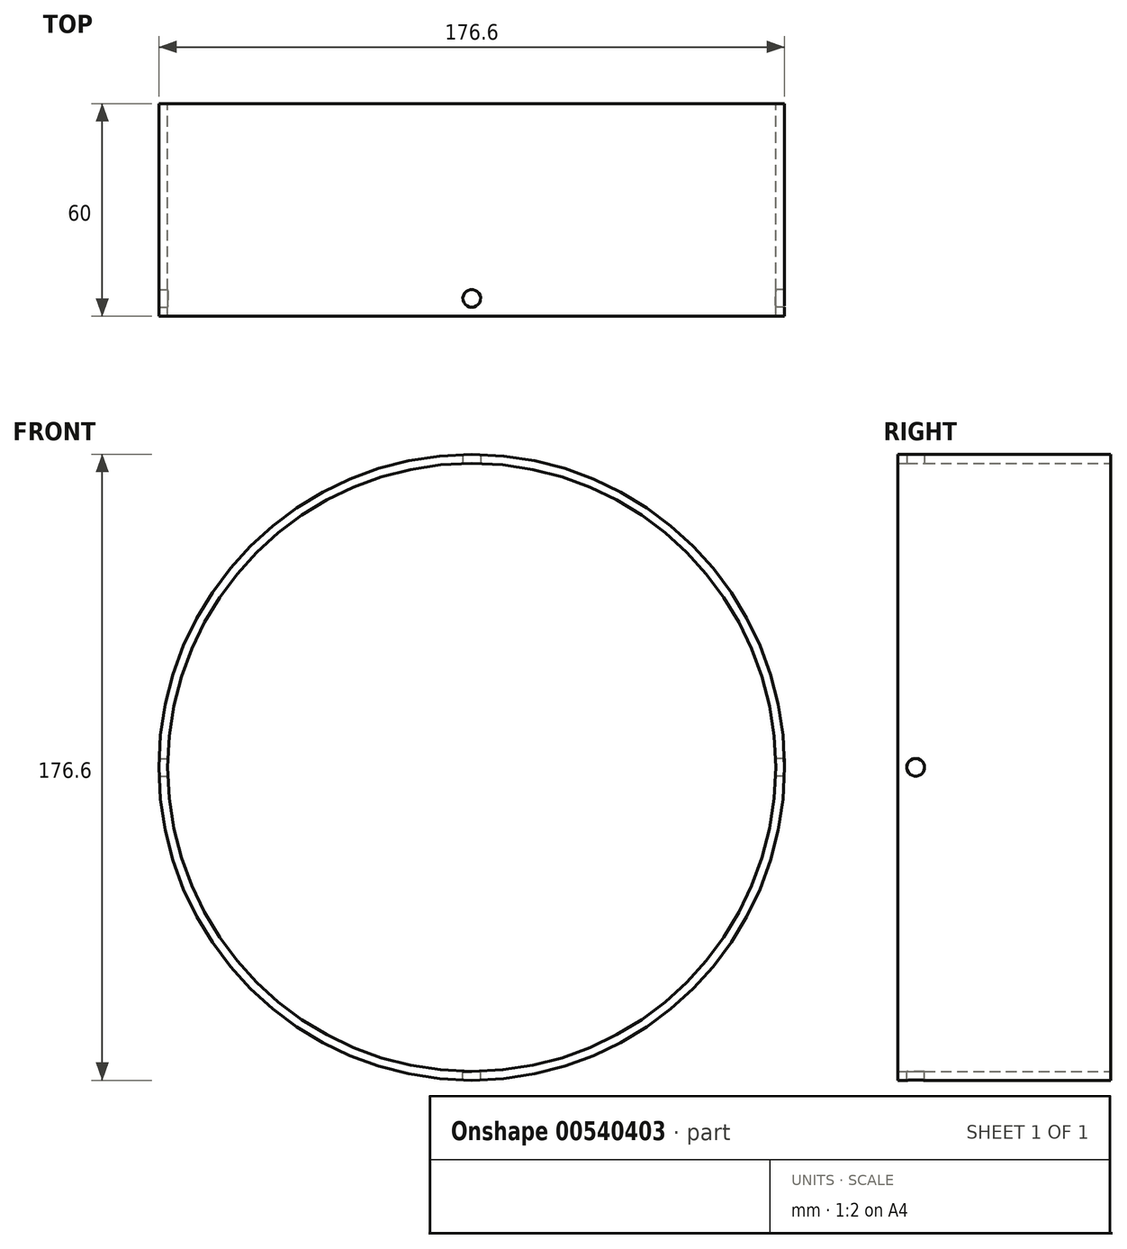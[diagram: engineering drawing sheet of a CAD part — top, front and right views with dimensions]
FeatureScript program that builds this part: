
annotation { "Feature Type Name" : "Feature", "Feature Type Description" : "" }
export const myFeature = defineFeature(function(context is Context, id is Id, definition is map)
    precondition{}
    {
        {
            var Q0;
            Q0=qCreatedBy(makeId("Front.planeOp"),FACE);
            var sketch = newSketch(context, id + "F0", { "sketchPlane" : qUnion([Q0])});
            skCircle(sketch, "E0", {"center": v(0, 0) * mm, "radius": 88.3 * mm});
            skCircle(sketch, "E1", {"center": v(0, 0) * mm, "radius": 85.8 * mm});
            skLineSegment(sketch, "E2", {"start": v(0, 0) * mm, "end": v(80, 0) * mm});
            skLineSegment(sketch, "E3", {"start": v(80, 0) * mm, "end": v(80, 31) * mm});
            skSolve(sketch);
        }
        {
            var Q0;
            Q0 = qSketchRegion(id + "F0", true);
            extrude(context, id + "F1", {"entities" : qUnion([Q0]), "depth" : 60 * mm, "offsetDistance" : 25 * mm});
        }
        {
            var Q0;
            Q0=qCreatedBy(makeId("Right.planeOp"),FACE);
            var sketch = newSketch(context, id + "F2", { "sketchPlane" : qUnion([Q0])});
            skLineSegment(sketch, "E4", {"start": v(0, 0) * mm, "end": v(-55, 0) * mm});
            skCircle(sketch, "E5", {"center": v(-55, 0) * mm, "radius": 2.5 * mm});
            skSolve(sketch);
        }
        {
            var Q0;
            Q0 = qSketchRegion(id + "F2", true);
            extrude(context, id + "F3", {"entities" : qUnion([Q0]), "operationType" : NewBodyOperationType.REMOVE, "oppositeDirection" : true, "depth" : 300 * mm, "offsetDistance" : 25 * mm});
        }
        {
            var Q0;
            Q0 = qSketchRegion(id + "F2", true);
            extrude(context, id + "F4", {"entities" : qUnion([Q0]), "operationType" : NewBodyOperationType.REMOVE, "depth" : 300 * mm, "offsetDistance" : 25 * mm});
        }
        {
            var Q0;
            Q0=qCreatedBy(makeId("Top.planeOp"),FACE);
            var sketch = newSketch(context, id + "F5", { "sketchPlane" : qUnion([Q0])});
            skLineSegment(sketch, "E6", {"start": v(0, 0) * mm, "end": v(0, -55) * mm});
            skCircle(sketch, "E7", {"center": v(0, -55) * mm, "radius": 2.5 * mm});
            skSolve(sketch);
        }
        {
            var Q0;
            Q0 = qSketchRegion(id + "F5", true);
            extrude(context, id + "F6", {"entities" : qUnion([Q0]), "operationType" : NewBodyOperationType.REMOVE, "oppositeDirection" : true, "depth" : 300 * mm, "offsetDistance" : 25 * mm});
        }
        {
            var Q0;
            Q0 = qSketchRegion(id + "F5", true);
            extrude(context, id + "F7", {"entities" : qUnion([Q0]), "operationType" : NewBodyOperationType.REMOVE, "depth" : 300 * mm, "offsetDistance" : 25 * mm});
        }
    });
